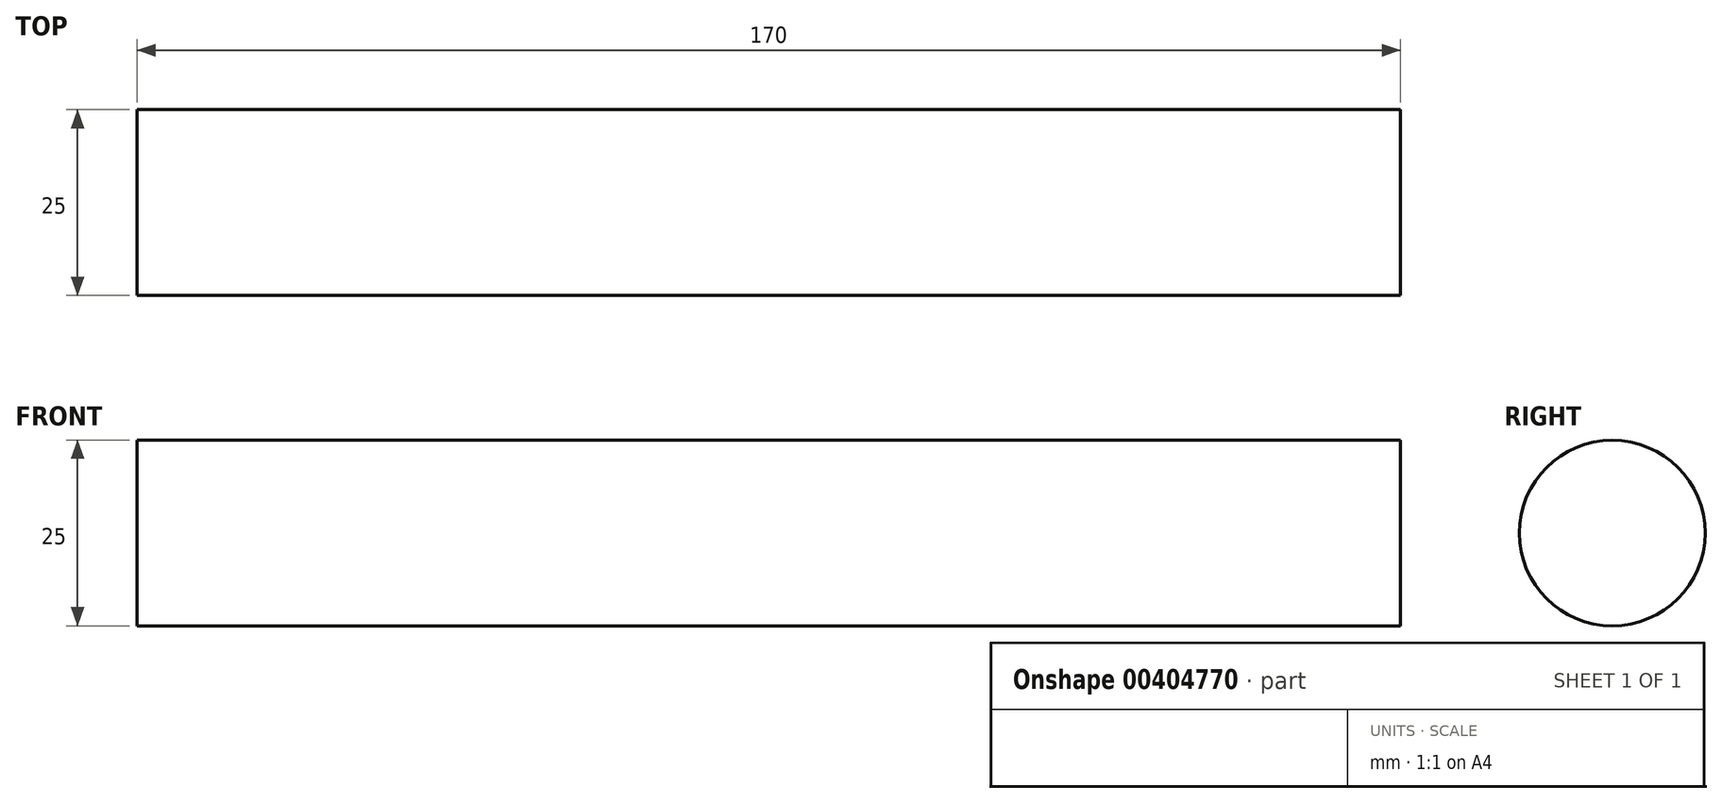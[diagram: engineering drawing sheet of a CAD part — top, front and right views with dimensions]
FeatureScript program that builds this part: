
annotation { "Feature Type Name" : "Feature", "Feature Type Description" : "" }
export const myFeature = defineFeature(function(context is Context, id is Id, definition is map)
    precondition{}
    {
        {
            var Q0;
            Q0=qCreatedBy(makeId("Right.planeOp"),FACE);
            var sketch = newSketch(context, id + "F0", { "sketchPlane" : qUnion([Q0])});
            skCircle(sketch, "E0", {"center": v(0, 0) * mm, "radius": 12.5 * mm});
            skSolve(sketch);
        }
        {
            var Q0;
            Q0=makeQuery(id+"F0.imprint","IMPRINT",FACE,{"disambiguationData":[TD([[makeQuery(id+"F0.imprint","IMPRINT",EDGE,{"derivedFrom":sQuery(id+"F0.wireOp",EDGE,"E0")}),1.0]])]});
            extrude(context, id + "F1", {"entities" : qUnion([Q0]), "depth" : 85 * mm, "hasSecondDirection" : true, "secondDirectionOppositeDirection" : true, "secondDirectionDepth" : 85 * mm});
        }
    });
